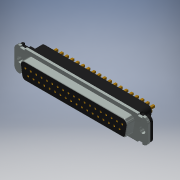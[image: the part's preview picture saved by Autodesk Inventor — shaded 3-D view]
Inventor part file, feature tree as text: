
AUTODESK INVENTOR PART (.ipt)
format: ipt  version: 2019 (Build 230136000, 136)  size: 653,312 bytes
history: native  units: mm (DEFAULTED — no unit token found)
features: extrude x14, pattern_linear x7, sketch x4, fillet x4, chamfer x3
ambient origin geometry x8: Origin, YZ Plane, XZ Plane, XY Plane, X Axis, Y Axis, Z Axis, Center Point
bodies: Solid1 (feature_tree)
feature tree (32):
  sketch  "Sketch1"  dims[d0=1.745329mm d6=0.381mm d7=2.418418mm d8=0.855895mm d9=2.418418mm]
  extrude  "Extrusion1"  Depth=0.381mm
  extrude  "Extrusion2"  Depth=1.397mm
  fillet  "Fillet4"  Radius=1.397mm
  extrude  "Pin1"  Depth=5.08mm TaperAngle=0.0deg
  extrude  "Pin2"  Depth=5.08mm TaperAngle=0.0deg
  extrude  "Pin50"  Depth=10.4394mm
  fillet  "Fillet1"  Radius=2.794mm
  fillet  "Fillet2"  Radius=180.0mm
  fillet  "Fillet50"  Radius=2.794mm
  extrude  "Extrusion5"  Depth=1.909443mm
  extrude  "Extrusion6"  Depth=0.254mm
  sketch  "Sketch4"  dims[d24=5.08mm d25=0.0mm d26=5.08mm d27=0.0mm d28=190.0mm d30=2.794mm d31=180.0mm d33=2.794mm d34=1.909443mm d35=0.254mm d36=1.6002mm d37=0.0mm d38=5.08mm d39=0.0mm d40=5.08mm d41=0.0mm d42=5.08mm d43=0.0mm d44=0.4953mm d45=0.4953mm d46=1.016mm d47=0.3048mm d48=0.3048mm d49=0.3048mm d50=0.3048mm d52=2.8448mm d53=5.08mm d54=0.0mm d55=0.4953mm d56=5.08mm d57=0.0mm d58=0.2032mm d59=0.2032mm d60=190.0mm d62=2.794mm d63=0.381mm d64=20.0mm d66=2.794mm d67=5.1054mm d68=0.0mm d69=5.6388mm d70=0.0mm d71=5.6388mm d72=0.0mm d73=5.6388mm d74=0.0mm d75=190.0mm d77=2.794mm d78=180.0mm d80=2.794mm d81=190.0mm d83=2.794mm d86=1.909443mm d87=10.4394mm d88=57.3786mm d89=45.0deg d90=45.0deg d91=45.0deg]
  extrude  "Extrusion7"  Depth=1.6002mm TaperAngle=0.0deg
  extrude  "Extrusion8"  Depth=5.08mm TaperAngle=0.0deg
  extrude  "ExtrudeSgr50"  Depth=5.08mm TaperAngle=0.0deg
  chamfer  "Chamfer1"  Distance=5.08mm
  chamfer  "Chamfer2"  Distance=0.4953mm
  chamfer  "Chamfer50"  Distance=0.4953mm
  pattern_linear  "Pattern1"  Spacing1=1.016mm  [1 undecoded]
  pattern_linear  "Pattern2"  Spacing1=0.3048mm  [1 undecoded]
  pattern_linear  "Pattern50"  Spacing1=0.3048mm  [1 undecoded]
  pattern_linear  "Pattern15"  Spacing1=0.3048mm  [1 undecoded]
  extrude  "Female"  Depth=10.4394mm
  extrude  "Socket1"  Depth=2.8448mm
  extrude  "Socket2"  Depth=5.08mm
  extrude  "Socket50"  TaperAngle=0.0deg  [1 undecoded]
  pattern_linear  "Pattern5"  Spacing1=0.4953mm  [1 undecoded]
  pattern_linear  "Pattern6"  Spacing1=5.08mm  [1 undecoded]
  pattern_linear  "Pattern7"  Spacing1=0.0mm  [1 undecoded]
  sketch  "Sketch2"  dims[d11=1.314425mm d15=2.54mm d19=1.397mm]
  sketch  "Sketch3"  dims[d20=1.27mm d21=0.0mm d22=5.08mm d23=0.0mm]
note: 8 required parameter values undecoded (feature->parameter linkage not recoverable at this tier; creation-order binding heuristic only, values carry confidence <= 0.55)
